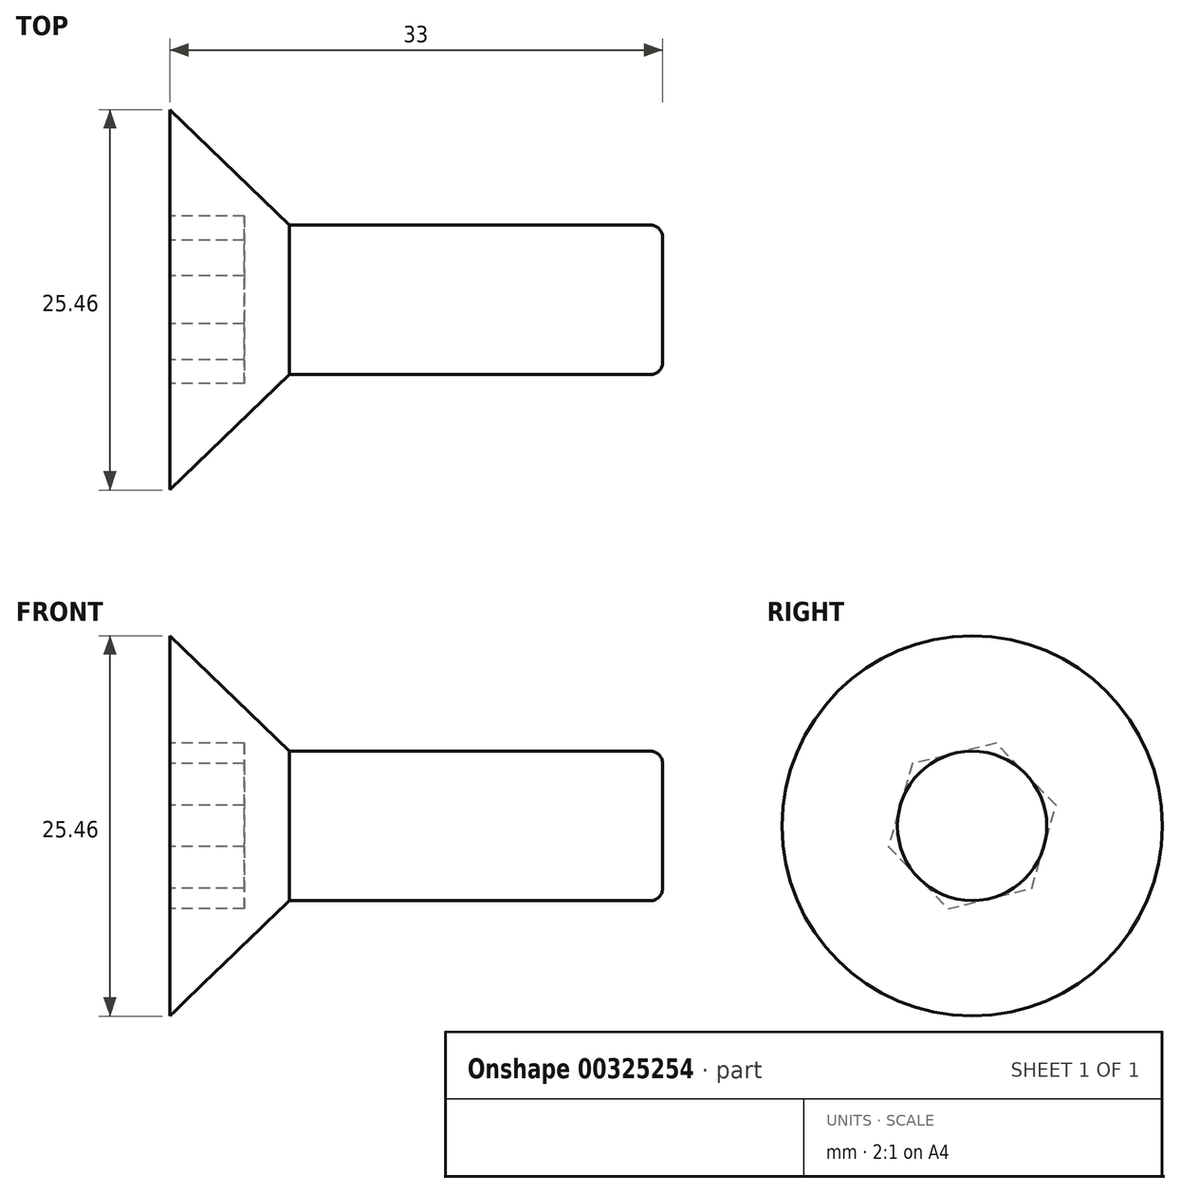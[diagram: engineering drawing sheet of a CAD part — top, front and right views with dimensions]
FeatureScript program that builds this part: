
annotation { "Feature Type Name" : "Feature", "Feature Type Description" : "" }
export const myFeature = defineFeature(function(context is Context, id is Id, definition is map)
    precondition{}
    {
        {
            var Q0;
            Q0=qCreatedBy(makeId("Front.planeOp"),FACE);
            var sketch = newSketch(context, id + "F0", { "sketchPlane" : qUnion([Q0])});
            skLineSegment(sketch, "E0", {"start": v(0, 0) * mm, "end": v(0, 12.73) * mm});
            skLineSegment(sketch, "E1", {"start": v(0, 12.73) * mm, "end": v(8, 5) * mm});
            skLineSegment(sketch, "E2", {"start": v(8, 5) * mm, "end": v(33, 5) * mm});
            skLineSegment(sketch, "E3", {"start": v(33, 5) * mm, "end": v(33, 0) * mm});
            skLineSegment(sketch, "E4", {"start": v(33, 0) * mm, "end": v(0, 0) * mm});
            skLineSegment(sketch, "E5", {"start": v(31.77, 0) * mm, "end": v(33, 0) * mm, "construction": true});
            skSolve(sketch);
        }
        {
            var Q0;
            Q0=makeQuery(id+"F0.imprint","IMPRINT",FACE,{"disambiguationData":[TD([[makeQuery(id+"F0.imprint","IMPRINT",EDGE,{"derivedFrom":sQuery(id+"F0.wireOp",EDGE,"E0")}),-1.0]])]});
            var Q1;
            Q1=sQuery(id+"F0.wireOp",EDGE,"E4");
            revolve(context, id + "F1", {"entities" : qUnion([Q0]), "axis" : qUnion([Q1]), "revolveType" : RevolveType.FULL});
        }
        {
            var Q0;
            Q0=makeQuery(id+"F1.opRevolve","SWEPT_FACE",FACE,{"disambiguationData":[OSD([sQuery(id+"F0.wireOp",EDGE,"E0")])]});
            var sketch = newSketch(context, id + "F2", { "sketchPlane" : qUnion([Q0])});
            skCircle(sketch, "E6.cCircle", {"center": v(0, 0) * mm, "radius": 5 * mm, "construction": true});
            skLineSegment(sketch, "E6.0", {"start": v(-1.61, 5.54) * mm, "end": v(4, 4.17) * mm});
            skLineSegment(sketch, "E6.1", {"start": v(4, 4.17) * mm, "end": v(5.6, -1.38) * mm});
            skLineSegment(sketch, "E6.2", {"start": v(5.6, -1.38) * mm, "end": v(1.61, -5.54) * mm});
            skLineSegment(sketch, "E6.3", {"start": v(1.61, -5.54) * mm, "end": v(-4, -4.17) * mm});
            skLineSegment(sketch, "E6.4", {"start": v(-4, -4.17) * mm, "end": v(-5.6, 1.38) * mm});
            skLineSegment(sketch, "E6.5", {"start": v(-5.6, 1.38) * mm, "end": v(-1.61, 5.54) * mm});
            skPoint(sketch, "E6.0.midPoint", {"position": v(1.2, 4.86) * mm});
            skSolve(sketch);
        }
        {
            var Q0;
            Q0=makeQuery(id+"F2.imprint","IMPRINT",FACE,{"disambiguationData":[TD([[makeQuery(id+"F2.imprint","IMPRINT",EDGE,{"derivedFrom":sQuery(id+"F2.wireOp",EDGE,"E6.0")}),-1.0]])]});
            extrude(context, id + "F3", {"entities" : qUnion([Q0]), "operationType" : NewBodyOperationType.REMOVE, "oppositeDirection" : true, "depth" : 5 * mm});
        }
        {
            var Q0;
            Q0=makeQuery(id+"F1.opRevolve","SWEPT_FACE",FACE,{"disambiguationData":[OSD([sQuery(id+"F0.wireOp",EDGE,"E3")])]});
            fillet(context, id + "F4", {"entities" : qUnion([Q0]), "radius" : 0.8 * mm, "tangentPropagation" : true, "allowEdgeOverflow" : false});
        }
    });
